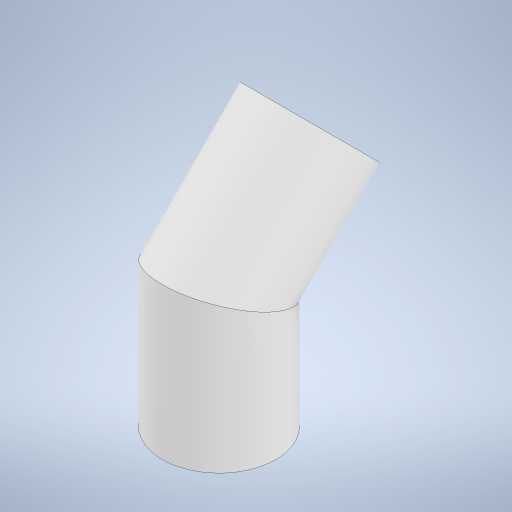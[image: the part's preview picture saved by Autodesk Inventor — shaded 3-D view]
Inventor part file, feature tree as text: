
AUTODESK INVENTOR PART (.ipt)
format: ipt  version: 2024 (Build 280153000, 153)  size: 321,024 bytes
history: native  units: in
note: dims shown in document units (in); Inventor stores cm internally (conversion verified against a paired STEP export)
features: revolve x2, extrude x2, other x1, sketch x1, plane x1, fillet x1
ambient origin geometry x8: Origin, YZ Plane, XZ Plane, XY Plane, X Axis, Y Axis, Z Axis, Center Point
bodies: Body1 (feature_tree)
feature tree (8):
  other  "Sólido1"
  sketch  "Boceto1"  dims[d0=1.1811in d1=0.0in d2=1.1811in d3=135.0deg d4=0.4724in d5=0.4724in d6=0.5246in d7=0.5246in d8=90.0deg d9=90.0deg d23=0.3937in d24=0.0in d25=0.3937in d26=0.0in d27=0.5906in]
  revolve  "Revolución1"  [1 undecoded]
  revolve  "Revolución2"  [1 undecoded]
  plane  "Plano de trabajo1"
  extrude  "Extrusión3"  TaperAngle=135.0deg  [1 undecoded]
  extrude  "Extrusión4"  Depth=0.4724in
  fillet  "Empalme1"  Radius=0.4724in
note: 3 required parameter values undecoded (feature->parameter linkage not recoverable at this tier; creation-order binding heuristic only, values carry confidence <= 0.55)